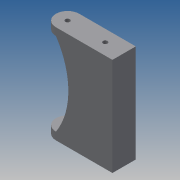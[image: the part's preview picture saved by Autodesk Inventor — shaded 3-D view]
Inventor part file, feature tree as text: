
AUTODESK INVENTOR PART (.ipt)
format: ipt  version: 2013 (Build 170138000, 138)  size: 116,736 bytes
history: native  units: mm
features: extrude x3, sketch x3, pattern_linear x1, mirror x1
ambient origin geometry x8: Origin, YZ Plane, XZ Plane, XY Plane, X Axis, Y Axis, Z Axis, Center Point
bodies: Solid1 (feature_tree)
feature tree (8):
  extrude  "Extrusion1"  Depth=50.0mm
  extrude  "Extrusion2"  Depth=31.0mm
  pattern_linear  "Rectangular Pattern1"  Count1=13  [1 undecoded]
  extrude  "Extrusion3"  Depth=10.0mm TaperAngle=0.0deg
  mirror  "Mirror1"
  sketch  "Sketch1"  dims[d0=6.0mm d2=50.0mm]
  sketch  "Sketch2"  dims[d3=15.0mm d4=31.0mm]
  sketch  "Sketch3"  dims[d5=10.0mm d6=0.0mm d7=130.0mm d8=10.0mm d9=0.0mm d10=20.0mm d12=120.0mm d13=100.0mm d15=2.0mm d16=0.0mm]
note: 1 required parameter value undecoded (feature->parameter linkage not recoverable at this tier; creation-order binding heuristic only, values carry confidence <= 0.55)
